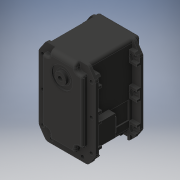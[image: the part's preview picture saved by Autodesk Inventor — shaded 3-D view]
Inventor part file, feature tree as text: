
AUTODESK INVENTOR PART (.ipt)
format: ipt  version: 2016 (Build 200138000, 138)  size: 716,288 bytes
history: native  units: in
note: dims shown in document units (in); Inventor stores cm internally (conversion verified against a paired STEP export)
features: other x3, sketch x3
ambient origin geometry x8: Origin, YZ Plane, XZ Plane, XY Plane, X Axis, Y Axis, Z Axis, Center Point
bodies: Solid1 (feature_tree)
feature tree (6):
  other  "MX-64T.ipt"
  other  "Solid1::MX-64T.ipt"
  other  "TaggingFeature1"
  sketch  "Sketch1"  dims[d0=0.3937in]
  sketch  "Sketch2"  dims[d2=0.1575in d3=0.0in d4=0.0in]
  sketch  "Sketch3"
